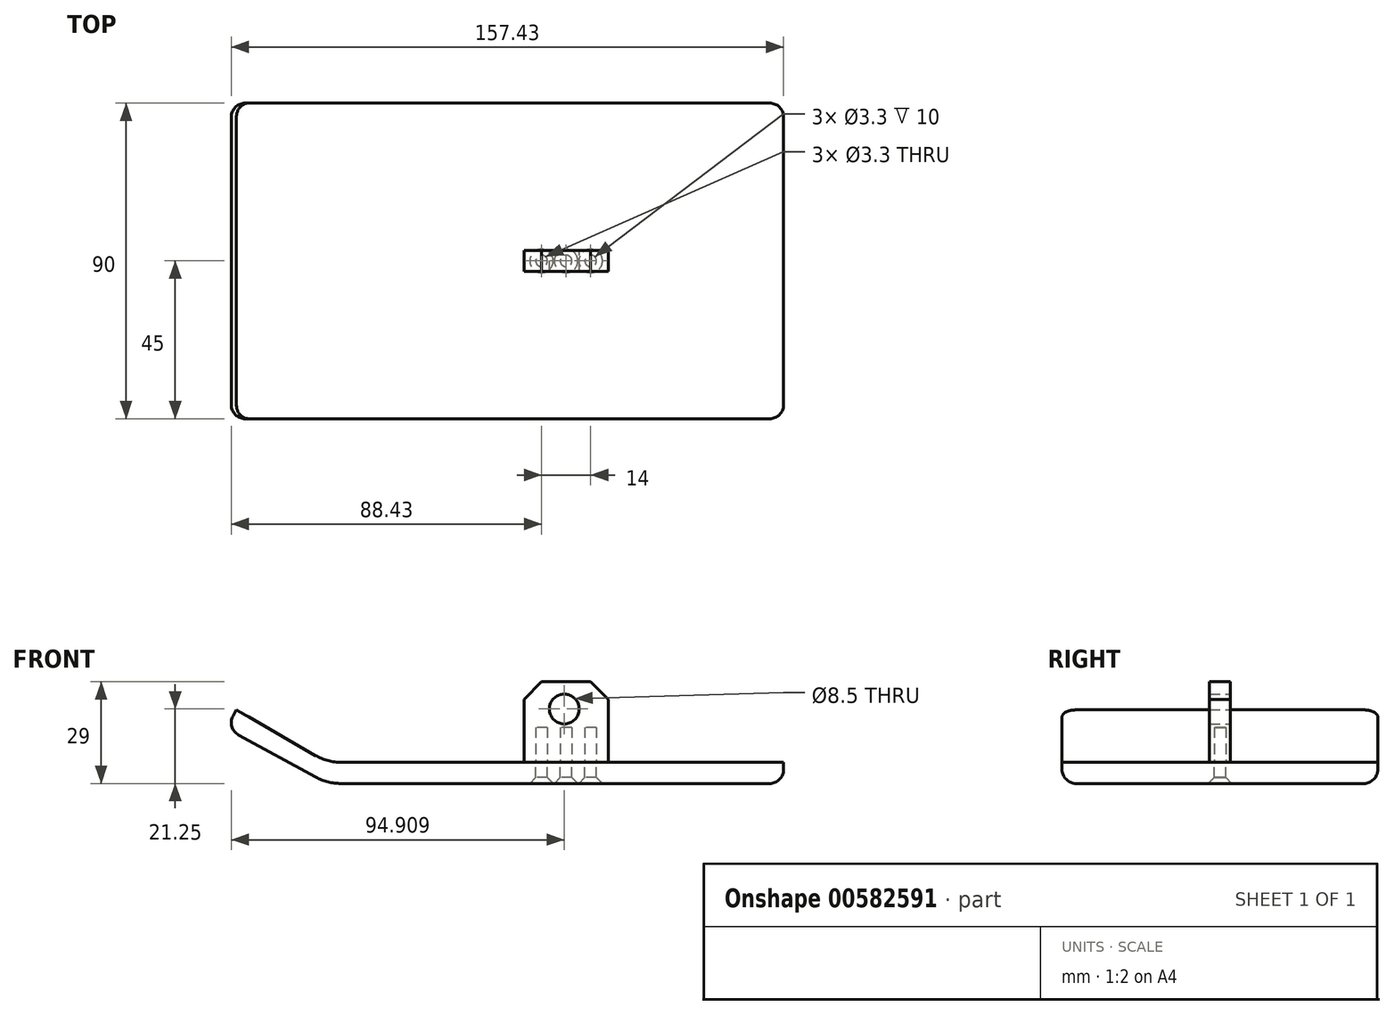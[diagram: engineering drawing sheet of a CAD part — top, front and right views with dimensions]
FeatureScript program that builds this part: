
annotation { "Feature Type Name" : "Feature", "Feature Type Description" : "" }
export const myFeature = defineFeature(function(context is Context, id is Id, definition is map)
    precondition{}
    {
        {
            var Q0;
            Q0=qCreatedBy(makeId("Front.planeOp"),FACE);
            var sketch = newSketch(context, id + "F0", { "sketchPlane" : qUnion([Q0])});
            skLineSegment(sketch, "E0.bottom", {"start": v(0, 0) * mm, "end": v(130, 0) * mm});
            skLineSegment(sketch, "E0.top", {"start": v(0, 6) * mm, "end": v(130, 6) * mm});
            skLineSegment(sketch, "E0.left", {"start": v(0, 0) * mm, "end": v(0, 6) * mm});
            skLineSegment(sketch, "E0.right", {"start": v(130, 0) * mm, "end": v(130, 6) * mm});
            skLineSegment(sketch, "E1", {"start": v(0, 0) * mm, "end": v(-28.85, 15.73) * mm});
            skLineSegment(sketch, "E2", {"start": v(-28.85, 15.73) * mm, "end": v(-25.98, 21) * mm});
            skLineSegment(sketch, "E3", {"start": v(-25.98, 21) * mm, "end": v(0, 6) * mm});
            skSolve(sketch);
        }
        {
            var Q0;
            Q0=makeQuery(id+"F0.imprint","IMPRINT",FACE,{"disambiguationData":[TD([[makeQuery(id+"F0.imprint","IMPRINT",EDGE,{"derivedFrom":sQuery(id+"F0.wireOp",EDGE,"E0.left")}),1.0]])]});
            var Q1;
            Q1=makeQuery(id+"F0.imprint","IMPRINT",FACE,{"disambiguationData":[TD([[makeQuery(id+"F0.imprint","IMPRINT",EDGE,{"derivedFrom":sQuery(id+"F0.wireOp",EDGE,"E0.bottom")}),1.0]])]});
            extrude(context, id + "F1", {"entities" : qUnion([Q0, Q1]), "endBound" : BoundingType.SYMMETRIC, "depth" : 90 * mm, "offsetDistance" : 25 * mm});
        }
        {
            var Q0;
            Q0=makeQuery(id+"F1.opExtrude","SWEPT_EDGE",EDGE,{"disambiguationData":[OSD([sQuery(id+"F0.wireOp",EDGE,"E0.top"),sQuery(id+"F0.wireOp",EDGE,"E0.left"),sQuery(id+"F0.wireOp",EDGE,"E3")])]});
            var Q1;
            Q1=makeQuery(id+"F1.opExtrude","SWEPT_EDGE",EDGE,{"disambiguationData":[OSD([sQuery(id+"F0.wireOp",EDGE,"E0.bottom"),sQuery(id+"F0.wireOp",EDGE,"E0.left"),sQuery(id+"F0.wireOp",EDGE,"E1")])]});
            fillet(context, id + "F2", {"entities" : qUnion([Q0, Q1]), "radius" : 15 * mm, "tangentPropagation" : true, "allowEdgeOverflow" : false});
        }
        {
            var Q0;
            Q0=makeQuery(id+"F1.opExtrude","CAP_EDGE",EDGE,{"disambiguationData":[OSD([sQuery(id+"F0.wireOp",EDGE,"E1")])],"isStart":false});
            var Q1;
            {var subQ0=sQuery(id+"F0.wireOp",EDGE,"E1");var subQ1=sQuery(id+"F0.wireOp",EDGE,"E0.bottom");Q1=makeQuery(id+"F2.opFillet","BLEND_EDGE",EDGE,{"blendedFrom":[makeQuery(id+"F1.opExtrude","SWEPT_EDGE",EDGE,{"disambiguationData":[OSD([subQ1,sQuery(id+"F0.wireOp",EDGE,"E0.left"),subQ0])]}),makeQuery(id+"F1.opExtrude","CAP_FACE",FACE,{"disambiguationData":[OSD([subQ1,sQuery(id+"F0.wireOp",EDGE,"E0.top"),sQuery(id+"F0.wireOp",EDGE,"E0.right"),subQ0,sQuery(id+"F0.wireOp",EDGE,"E2"),sQuery(id+"F0.wireOp",EDGE,"E3")])],"isStart":false})],"blendedInto":[makeQuery(id+"F1.opExtrude","CAP_FACE",FACE,{"disambiguationData":[OSD([subQ1,sQuery(id+"F0.wireOp",EDGE,"E0.top"),sQuery(id+"F0.wireOp",EDGE,"E0.right"),subQ0,sQuery(id+"F0.wireOp",EDGE,"E2"),sQuery(id+"F0.wireOp",EDGE,"E3")])],"isStart":false})]});}
            var Q2;
            Q2=makeQuery(id+"F1.opExtrude","CAP_EDGE",EDGE,{"disambiguationData":[OSD([sQuery(id+"F0.wireOp",EDGE,"E0.bottom")])],"isStart":false});
            var Q3;
            Q3=makeQuery(id+"F1.opExtrude","CAP_EDGE",EDGE,{"disambiguationData":[OSD([sQuery(id+"F0.wireOp",EDGE,"E0.bottom")])],"isStart":true});
            var Q4;
            {var subQ0=sQuery(id+"F0.wireOp",EDGE,"E1");var subQ1=sQuery(id+"F0.wireOp",EDGE,"E0.bottom");Q4=makeQuery(id+"F2.opFillet","BLEND_EDGE",EDGE,{"blendedFrom":[makeQuery(id+"F1.opExtrude","SWEPT_EDGE",EDGE,{"disambiguationData":[OSD([subQ1,sQuery(id+"F0.wireOp",EDGE,"E0.left"),subQ0])]}),makeQuery(id+"F1.opExtrude","CAP_FACE",FACE,{"disambiguationData":[OSD([subQ1,sQuery(id+"F0.wireOp",EDGE,"E0.top"),sQuery(id+"F0.wireOp",EDGE,"E0.right"),subQ0,sQuery(id+"F0.wireOp",EDGE,"E2"),sQuery(id+"F0.wireOp",EDGE,"E3")])],"isStart":true})],"blendedInto":[makeQuery(id+"F1.opExtrude","CAP_FACE",FACE,{"disambiguationData":[OSD([subQ1,sQuery(id+"F0.wireOp",EDGE,"E0.top"),sQuery(id+"F0.wireOp",EDGE,"E0.right"),subQ0,sQuery(id+"F0.wireOp",EDGE,"E2"),sQuery(id+"F0.wireOp",EDGE,"E3")])],"isStart":true})]});}
            var Q5;
            Q5=makeQuery(id+"F1.opExtrude","CAP_EDGE",EDGE,{"disambiguationData":[OSD([sQuery(id+"F0.wireOp",EDGE,"E1")])],"isStart":true});
            fillet(context, id + "F3", {"entities" : qUnion([Q0, Q1, Q2, Q3, Q4, Q5]), "radius" : 4 * mm, "tangentPropagation" : true, "allowEdgeOverflow" : false});
        }
        {
            var Q0;
            Q0=makeQuery(id+"F1.opExtrude","SWEPT_FACE",FACE,{"disambiguationData":[OSD([sQuery(id+"F0.wireOp",EDGE,"E0.top")])]});
            var sketch = newSketch(context, id + "F4", { "sketchPlane" : qUnion([Q0])});
            skLineSegment(sketch, "E4.bottom", {"start": v(56, -3) * mm, "end": v(80, -3) * mm});
            skLineSegment(sketch, "E4.top", {"start": v(56, 3) * mm, "end": v(80, 3) * mm});
            skLineSegment(sketch, "E4.left", {"start": v(56, -3) * mm, "end": v(56, 3) * mm});
            skLineSegment(sketch, "E4.right", {"start": v(80, -3) * mm, "end": v(80, 3) * mm});
            skSolve(sketch);
        }
        {
            var Q0;
            Q0=makeQuery(id+"F4.imprint","IMPRINT",FACE,{"disambiguationData":[TD([[makeQuery(id+"F4.imprint","IMPRINT",EDGE,{"derivedFrom":sQuery(id+"F4.wireOp",EDGE,"E4.bottom")}),1.0]])]});
            extrude(context, id + "F5", {"entities" : qUnion([Q0]), "depth" : 23 * mm, "offsetDistance" : 25 * mm});
        }
        {
            var Q0;
            Q0=makeQuery(id+"F5.opExtrude","CAP_EDGE",EDGE,{"disambiguationData":[OSD([sQuery(id+"F4.wireOp",EDGE,"E4.right")])],"isStart":false});
            var Q1;
            Q1=makeQuery(id+"F5.opExtrude","CAP_EDGE",EDGE,{"disambiguationData":[OSD([sQuery(id+"F4.wireOp",EDGE,"E4.left")])],"isStart":false});
            chamfer(context, id + "F6", {"entities" : qUnion([Q0, Q1]), "width" : 5 * mm, "tangentPropagation" : true});
        }
        {
            var Q0;
            Q0=makeQuery(id+"F5.opExtrude","SWEPT_FACE",FACE,{"disambiguationData":[OSD([sQuery(id+"F4.wireOp",EDGE,"E4.top")])]});
            var sketch = newSketch(context, id + "F7", { "sketchPlane" : qUnion([Q0])});
            skCircle(sketch, "E5", {"center": v(-67.48, 21.25) * mm, "radius": 4.25 * mm});
            skSolve(sketch);
        }
        {
            var Q0;
            Q0=makeQuery(id+"F7.imprint","IMPRINT",FACE,{"disambiguationData":[TD([[makeQuery(id+"F7.imprint","IMPRINT",EDGE,{"derivedFrom":sQuery(id+"F7.wireOp",EDGE,"E5")}),1.0]])]});
            extrude(context, id + "F8", {"entities" : qUnion([Q0]), "operationType" : NewBodyOperationType.REMOVE, "endBound" : BoundingType.SYMMETRIC, "oppositeDirection" : true, "depth" : 25 * mm, "offsetDistance" : 25 * mm});
        }
        {
            var Q0;
            Q0=makeQuery(id+"F1.opExtrude","SWEPT_EDGE",EDGE,{"disambiguationData":[OSD([sQuery(id+"F0.wireOp",EDGE,"E1"),sQuery(id+"F0.wireOp",EDGE,"E2")])]});
            var Q1;
            Q1=makeQuery(id+"F1.opExtrude","SWEPT_EDGE",EDGE,{"disambiguationData":[OSD([sQuery(id+"F0.wireOp",EDGE,"E0.bottom"),sQuery(id+"F0.wireOp",EDGE,"E0.right")])]});
            fillet(context, id + "F9", {"entities" : qUnion([Q0, Q1]), "radius" : 4 * mm, "tangentPropagation" : true, "allowEdgeOverflow" : false});
        }
        {
            var Q0;
            Q0=makeQuery(id+"F4.imprint","IMPRINT",FACE,{"disambiguationData":[TD([[makeQuery(id+"F4.imprint","IMPRINT",EDGE,{"derivedFrom":sQuery(id+"F4.wireOp",EDGE,"E4.bottom")}),1.0]])]});
            var sketch = newSketch(context, id + "F10", { "sketchPlane" : qUnion([Q0])});
            skPoint(sketch, "E6", {"position": v(75, 0) * mm});
            skCircle(sketch, "E7", {"center": v(75, 0) * mm, "radius": 1.65 * mm});
            skCircle(sketch, "E8", {"center": v(61, 0) * mm, "radius": 1.65 * mm});
            skCircle(sketch, "E9", {"center": v(68, 0) * mm, "radius": 1.65 * mm});
            skSolve(sketch);
        }
        {
            var Q0;
            Q0=makeQuery(id+"F10.imprint","IMPRINT",FACE,{"disambiguationData":[TD([[makeQuery(id+"F10.imprint","IMPRINT",EDGE,{"derivedFrom":sQuery(id+"F10.wireOp",EDGE,"E7")}),1.0]])]});
            var Q1;
            Q1=makeQuery(id+"F10.imprint","IMPRINT",FACE,{"disambiguationData":[TD([[makeQuery(id+"F10.imprint","IMPRINT",EDGE,{"derivedFrom":sQuery(id+"F10.wireOp",EDGE,"E9")}),1.0]])]});
            var Q2;
            Q2=makeQuery(id+"F10.imprint","IMPRINT",FACE,{"disambiguationData":[TD([[makeQuery(id+"F10.imprint","IMPRINT",EDGE,{"derivedFrom":sQuery(id+"F10.wireOp",EDGE,"E8")}),1.0]])]});
            extrude(context, id + "F11", {"entities" : qUnion([Q0, Q1, Q2]), "operationType" : NewBodyOperationType.REMOVE, "depth" : 10 * mm, "offsetDistance" : 25 * mm});
        }
        {
            var Q0;
            Q0 = qSketchRegion(id + "F10", true);
            extrude(context, id + "F12", {"entities" : qUnion([Q0]), "operationType" : NewBodyOperationType.REMOVE, "oppositeDirection" : true, "depth" : 10 * mm, "offsetDistance" : 25 * mm});
        }
        {
            var Q0;
            Q0=makeQuery(id+"F12.boolean.opBoolean","INTERSECT",EDGE,{"derivedFrom":[makeQuery(id+"F1.opExtrude","SWEPT_FACE",FACE,{"disambiguationData":[OSD([sQuery(id+"F0.wireOp",EDGE,"E0.bottom")])]}),makeQuery(id+"F12.opExtrude","SWEPT_FACE",FACE,{"disambiguationData":[OSD([sQuery(id+"F10.wireOp",EDGE,"E8")])]})]});
            var Q1;
            Q1=makeQuery(id+"F12.boolean.opBoolean","INTERSECT",EDGE,{"derivedFrom":[makeQuery(id+"F1.opExtrude","SWEPT_FACE",FACE,{"disambiguationData":[OSD([sQuery(id+"F0.wireOp",EDGE,"E0.bottom")])]}),makeQuery(id+"F12.opExtrude","SWEPT_FACE",FACE,{"disambiguationData":[OSD([sQuery(id+"F10.wireOp",EDGE,"E9")])]})]});
            var Q2;
            Q2=makeQuery(id+"F12.boolean.opBoolean","INTERSECT",EDGE,{"derivedFrom":[makeQuery(id+"F1.opExtrude","SWEPT_FACE",FACE,{"disambiguationData":[OSD([sQuery(id+"F0.wireOp",EDGE,"E0.bottom")])]}),makeQuery(id+"F12.opExtrude","SWEPT_FACE",FACE,{"disambiguationData":[OSD([sQuery(id+"F10.wireOp",EDGE,"E7")])]})]});
            var Q3;
            Q3=makeQuery(id+"F1.opExtrude","SWEPT_FACE",FACE,{"disambiguationData":[OSD([sQuery(id+"F0.wireOp",EDGE,"E0.bottom")])]});
            chamfer(context, id + "F13", {"entities" : qUnion([Q0, Q1, Q2, Q3]), "width" : 1.7 * mm});
        }
    });
